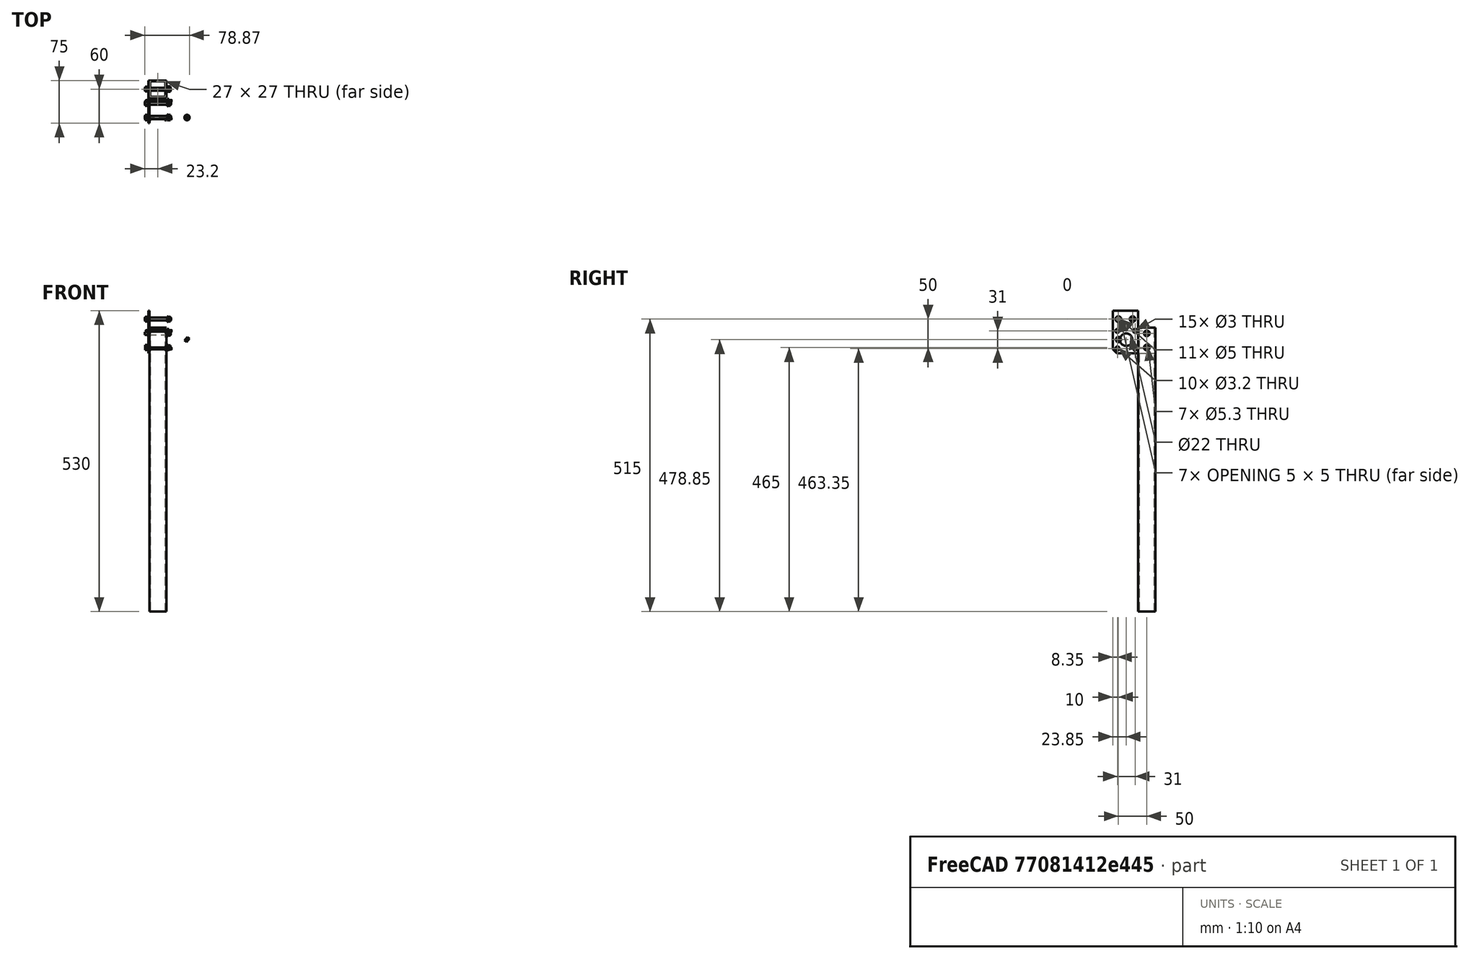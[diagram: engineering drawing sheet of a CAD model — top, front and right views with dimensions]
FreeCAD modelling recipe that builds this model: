
FCSTD DOCUMENT  (FreeCAD 0.21R33694 (Git))
Label: example
License: All rights reserved
LicenseURL: http://en.wikipedia.org/wiki/All_rights_reserved
objects: Part::FeaturePython×49, Part::Feature×18, App::DocumentObjectGroupPython×16, Part::Cylinder×1, PartDesign::Pocket×1, Part::Thickness×1
note: 71 computed .brp shape members not serialized (recipe doc carries the construction recipe); baked Part::Feature solids carry a one-line shape summary decoded from their .brp

FEATURE [Part::FeaturePython] Clone053  label="Clone of Hexagon nut ISO4032 - M010"  # WARN: FeaturePython — macro-defined, semantics opaque (R4)
  Placement = pos=(53.1534,405,-17.3076) rot=(0,-1,0;0.890118rad)
  Scale = (1,1,1)
FEATURE [Part::FeaturePython] Clone062  label="Clone of Clone of Clone of Clone of Clone of Plain washer ISO7089 - M010"  # WARN: FeaturePython — macro-defined, semantics opaque (R4)
  Placement = pos=(17.5,405,20) rot=(0.57735,0.57735,-0.57735;4.18879rad)
  Scale = (1,1,1)
FEATURE [Part::Cylinder] Cylinder001  label="Cilindro001"
  Angle = 360
  AttacherType = Attacher::AttachEngine3D
  FirstAngle = 0
  Height = 45
  Placement = pos=(-21,403.35,-0.65) rot=(0.57735,-0.57735,0.57735;4.18879rad)
  Radius = 1.5
  SecondAngle = 0
FEATURE [Part::FeaturePython] Clone029  label="Clone of Cilindro005"  # Draft clone (typed FeaturePython)
  Objects = -> [Cylinder001]
  Placement = pos=(-21,403.35,-31.65) rot=(0.57735,-0.57735,0.57735;4.18879rad)
  Scale = (1,1,1)
FEATURE [Part::Feature] BOLTS_part002  label="Hexagon nut ISO4032 - M3"
  Placement = pos=(17,434.35,-31.65) rot=(-0.383062,-0.840552,-0.383062;4.53956rad)
  shape: bbox 2.4 x 6.234 x 6.005 mm, 9 faces (baked)
FEATURE [Part::FeaturePython] Clone068  label="Clone of Hexagon nut ISO4032 - M014"  # Draft clone (typed FeaturePython)
  Objects = -> [BOLTS_part002]
  Placement = pos=(19.4,403.35,-0.65) rot=(-0.383062,0.840552,0.383062;4.53956rad)
  Scale = (1,1,1)
FEATURE [Part::FeaturePython] Clone081  label="Clone of Hexagon nut ISO4032 - M020"  # Draft clone (typed FeaturePython)
  Objects = -> [BOLTS_part002]
  Placement = pos=(19.4,403.35,-31.65) rot=(-0.383062,0.840552,0.383062;4.53956rad)
  Scale = (1,1,1)
FEATURE [Part::Feature] BOLTS_part004  label="Plain washer ISO7089 - M3"
  Placement = pos=(17,434.35,-31.65) rot=(0,-1,0;1.5708rad)
  shape: bbox 0.5 x 7 x 7 mm, 4 faces (baked)
FEATURE [Part::FeaturePython] Clone074  label="Clone of Plain washer ISO7089 - M3"  # Draft clone (typed FeaturePython)
  Objects = -> [BOLTS_part004]
  Placement = pos=(17,403.35,-0.65) rot=(0,-1,0;1.5708rad)
  Scale = (1,1,1)
FEATURE [Part::FeaturePython] Clone080  label="Clone of Plain washer ISO7089 - M012"  # Draft clone (typed FeaturePython)
  Objects = -> [BOLTS_part004]
  Placement = pos=(17,403.35,-31.65) rot=(0,-1,0;1.5708rad)
  Scale = (1,1,1)
FEATURE [Part::FeaturePython] Clone031  label="Clone of Cilindro007"  # Draft clone (typed FeaturePython)
  Objects = -> [Cylinder001]
  Placement = pos=(-21,434.35,-31.65) rot=(0.57735,-0.57735,0.57735;4.18879rad)
  Scale = (1,1,1)
FEATURE [Part::FeaturePython] Clone030  label="Clone of Cilindro006"  # Draft clone (typed FeaturePython)
  Objects = -> [Cylinder001]
  Placement = pos=(-21,434.35,-0.65) rot=(0.57735,-0.57735,0.57735;4.18879rad)
  Scale = (1,1,1)
FEATURE [Part::FeaturePython] Clone067  label="Clone of Hexagon nut ISO4032 - M3"  # Draft clone (typed FeaturePython)
  Objects = -> [BOLTS_part002]
  Placement = pos=(19.4,434.35,-0.65) rot=(-0.383062,0.840552,0.383062;4.53956rad)
  Scale = (1,1,1)
FEATURE [Part::FeaturePython] Clone075  label="Clone of Plain washer ISO7089 - M007"  # Draft clone (typed FeaturePython)
  Objects = -> [BOLTS_part004]
  Placement = pos=(17,434.35,-0.65) rot=(0,-1,0;1.5708rad)
  Scale = (1,1,1)
FEATURE [Part::FeaturePython] Clone090  # WARN: FeaturePython — macro-defined, semantics opaque (R4)
FEATURE [Part::FeaturePython] Clone050  label="Clone of Hexagon nut ISO4032 - M007"  # WARN: FeaturePython — macro-defined, semantics opaque (R4)
  Placement = pos=(22.2,430,20) rot=(0,1,0;4.71239rad)
  Scale = (1,1,1)
FEATURE [Part::FeaturePython] Clone061  label="Clone of Clone of Clone of Clone of Clone of Plain washer ISO7089 - M009"  # WARN: FeaturePython — macro-defined, semantics opaque (R4)
  Placement = pos=(17.5,430,20) rot=(0,-1,0;1.5708rad)
  Scale = (1,1,1)
FEATURE [Part::FeaturePython] Clone052  label="Clone of Hexagon nut ISO4032 - M009"  # WARN: FeaturePython — macro-defined, semantics opaque (R4)
  Placement = pos=(22.2,455,-5) rot=(0,1,0;4.71239rad)
  Scale = (1,1,1)
FEATURE [Part::FeaturePython] Clone060  label="Clone of Clone of Clone of Clone of Clone of Plain washer ISO7089 - M008"  # WARN: FeaturePython — macro-defined, semantics opaque (R4)
  Placement = pos=(17.5,455,-5) rot=(0,-1,0;1.5708rad)
  Scale = (1,1,1)
FEATURE [Part::FeaturePython] Clone051  label="Clone of Hexagon nut ISO4032 - M008"  # WARN: FeaturePython — macro-defined, semantics opaque (R4)
  Placement = pos=(22.2,455,-30) rot=(0,1,0;4.71239rad)
  Scale = (1,1,1)
FEATURE [Part::FeaturePython] Clone059  label="Clone of Clone of Clone of Clone of Clone of Plain washer ISO7089 - M007"  # WARN: FeaturePython — macro-defined, semantics opaque (R4)
  Placement = pos=(17.5,455,-30) rot=(0,-1,0;1.5708rad)
  Scale = (1,1,1)
FEATURE [Part::FeaturePython] Clone089  label="Clone of Clone of Cilindro003"  # WARN: FeaturePython — macro-defined, semantics opaque (R4)
  Placement = pos=(-22.8,455,-30) rot=(0,1,0;1.5708rad)
  Scale = (1,1,1)
FEATURE [Part::FeaturePython] Clone091  label="Clone of Clone of Clone of Cilindro004"  # Draft clone (typed FeaturePython)
  Objects = -> [Clone089]
  Placement = pos=(-22.8,405,20) rot=(0,1,0;1.5708rad)
  Scale = (1,1,1)
FEATURE [Part::FeaturePython] Clone092  label="Clone of Clone of Clone of Cilindro005"  # Draft clone (typed FeaturePython)
  Objects = -> [Clone089]
  Placement = pos=(-23.2,455,-5) rot=(0,1,0;1.5708rad)
  Scale = (1,1,1)
FEATURE [PartDesign::Pocket] Pocket005
  AllowMultiFace = false
  Direction = (1,1,1)
  Length = 5
  Length2 = 5
  Placement = pos=(16.1113,-0.661292,-3.33e-14) rot=(-0.57735,0.57735,0.57735;4.18879rad)
  Type = 0
FEATURE [Part::FeaturePython] Clone028  label="Clone of Pocket005"  # Draft clone (typed FeaturePython)
  Objects = -> [Pocket005]
  Placement = pos=(-15,0,0) rot=(0.57735,-0.57735,-0.57735;2.0944rad)
  Scale = (1,1,1)
FEATURE [Part::FeaturePython] Clone076  label="Clone of Plain washer ISO7089 - M008"  # Draft clone (typed FeaturePython)
  Objects = -> [BOLTS_part004]
  Placement = pos=(15,403.35,-31.65) rot=(0,-1,0;1.5708rad)
  Scale = (1,1,1)
FEATURE [Part::FeaturePython] Clone070  label="Clone of Hexagon nut ISO4032 - M016"  # Draft clone (typed FeaturePython)
  Objects = -> [BOLTS_part002]
  Placement = pos=(14.5,403.35,-31.65) rot=(0,-1,0;1.5708rad)
  Scale = (1,1,1)
FEATURE [Part::FeaturePython] Clone078  label="Clone of Plain washer ISO7089 - M010"  # Draft clone (typed FeaturePython)
  Objects = -> [BOLTS_part004]
  Placement = pos=(15,434.35,-31.65) rot=(0,-1,0;1.5708rad)
  Scale = (1,1,1)
FEATURE [Part::FeaturePython] Clone069  label="Clone of Hexagon nut ISO4032 - M015"  # Draft clone (typed FeaturePython)
  Objects = -> [BOLTS_part002]
  Placement = pos=(14.5,434.35,-31.65) rot=(0,-1,0;1.5708rad)
  Scale = (1,1,1)
FEATURE [Part::FeaturePython] Clone079  label="Clone of Plain washer ISO7089 - M011"  # Draft clone (typed FeaturePython)
  Objects = -> [BOLTS_part004]
  Placement = pos=(15,434.35,-0.65) rot=(0,-1,0;1.5708rad)
  Scale = (1,1,1)
FEATURE [Part::FeaturePython] Clone072  label="Clone of Hexagon nut ISO4032 - M018"  # Draft clone (typed FeaturePython)
  Objects = -> [BOLTS_part002]
  Placement = pos=(14.5,434.35,-0.65) rot=(0,-1,0;1.5708rad)
  Scale = (1,1,1)
FEATURE [Part::FeaturePython] Clone077  label="Clone of Plain washer ISO7089 - M009"  # Draft clone (typed FeaturePython)
  Objects = -> [BOLTS_part004]
  Placement = pos=(15,403.35,-0.65) rot=(0,-1,0;1.5708rad)
  Scale = (1,1,1)
FEATURE [Part::FeaturePython] Clone071  label="Clone of Hexagon nut ISO4032 - M017"  # Draft clone (typed FeaturePython)
  Objects = -> [BOLTS_part002]
  Placement = pos=(14.5,403.35,-0.65) rot=(0,-1,0;1.5708rad)
  Scale = (1,1,1)
FEATURE [Part::FeaturePython] Clone087  label="Clone of Clone of Hexagon nut ISO4032 - M020"  # WARN: FeaturePython — macro-defined, semantics opaque (R4)
  Placement = pos=(-12.1,403.35,-31.65) rot=(0,1,0;4.71239rad)
  Scale = (1,1,1)
FEATURE [Part::FeaturePython] Clone088  label="Clone of Clone of Hexagon nut ISO4032 - M021"  # WARN: FeaturePython — macro-defined, semantics opaque (R4)
  Placement = pos=(-12.1,434.35,-31.65) rot=(0,1,0;4.71239rad)
  Scale = (1,1,1)
FEATURE [Part::FeaturePython] Clone082  label="Clone of Clone of Plain washer ISO7089 - M012"  # Draft clone (typed FeaturePython)
  Objects = -> [Clone080]
  Placement = pos=(-14.5,434.35,-31.65) rot=(0,-1,0;1.5708rad)
  Scale = (1,1,1)
FEATURE [Part::FeaturePython] Clone085  label="Clone of Clone of Plain washer ISO7089 - M015"  # Draft clone (typed FeaturePython)
  Objects = -> [Clone080]
  Placement = pos=(-14.5,403.35,-0.65) rot=(0,-1,0;1.5708rad)
  Scale = (1,1,1)
FEATURE [Part::Feature] Fusion002  label="Nema17+Pulley002"
  Placement = pos=(-63.5,418.85,-16.15) rot=(1,0,0;3.14159rad)
  shape: bbox 71 x 42.3 x 42.3 mm, 115 faces (baked)
FEATURE [Part::FeaturePython] Clone056  label="Clone of Hexagon nut ISO4032 - M013"  # WARN: FeaturePython — macro-defined, semantics opaque (R4)
  Placement = pos=(-22.2,455,-30) rot=(0.185846,-0.964843,0.185846;4.67661rad)
  Scale = (1,1,1)
FEATURE [Part::FeaturePython] Clone054  label="Clone of Hexagon nut ISO4032 - M011"  # WARN: FeaturePython — macro-defined, semantics opaque (R4)
  Placement = pos=(-17.5,455,-5) rot=(0,1,0;4.71239rad)
  Scale = (1,1,1)
FEATURE [Part::FeaturePython] Clone057  label="Clone of Clone of Hexagon nut ISO4032 - M011"  # Draft clone (typed FeaturePython)
  Objects = -> [Clone054]
  Placement = pos=(-17.5,405,20) rot=(0,1,0;4.71239rad)
  Scale = (1,1,1)
FEATURE [Part::FeaturePython] Clone063  label="Clone of Clone of Clone of Clone of Clone of Plain washer ISO7089 - M011"  # WARN: FeaturePython — macro-defined, semantics opaque (R4)
  Placement = pos=(-16.5,405,20) rot=(0,-1,0;1.5708rad)
  Scale = (1,1,1)
FEATURE [Part::FeaturePython] Clone093  label="Clone of Clone of Clone of Cilindro003"  # Draft clone (typed FeaturePython)
  Objects = -> [Clone089]
  Placement = pos=(-22.8,430,20) rot=(0,1,0;1.5708rad)
  Scale = (1,1,1)
FEATURE [Part::FeaturePython] Clone055  label="Clone of Hexagon nut ISO4032 - M012"  # WARN: FeaturePython — macro-defined, semantics opaque (R4)
  Placement = pos=(-17.5,430,20) rot=(0,1,0;4.71239rad)
  Scale = (1,1,1)
FEATURE [Part::FeaturePython] Clone064  label="Clone of Clone of Clone of Clone of Clone of Plain washer ISO7089 - M012"  # WARN: FeaturePython — macro-defined, semantics opaque (R4)
  Placement = pos=(-16.5,430,20) rot=(0,-1,0;1.5708rad)
  Scale = (1,1,1)
FEATURE [Part::FeaturePython] Clone065  label="Clone of Clone of Clone of Clone of Clone of Clone of Plain washer ISO7089 - M012"  # Draft clone (typed FeaturePython)
  Objects = -> [Clone064]
  Placement = pos=(-16.5,455,-30) rot=(0,-1,0;1.5708rad)
  Scale = (1,1,1)
FEATURE [Part::FeaturePython] Clone066  label="Clone of Clone of Clone of Clone of Clone of Clone of Plain washer ISO7089 - M013"  # Draft clone (typed FeaturePython)
  Objects = -> [Clone064]
  Placement = pos=(-16.5,455,-5) rot=(0,-1,0;1.5708rad)
  Scale = (1,1,1)
FEATURE [Part::Thickness] Thickness
  Intersection = false
  Join = 0
  Mode = 0
  SelfIntersection = false
  Value = -1.5
FEATURE [Part::FeaturePython] Clone023  label="Clone of Thickness001"  # Draft clone (typed FeaturePython)
  Objects = -> [Thickness]
  Placement = pos=(0,475,-465) rot=(1,0,0;1.5708rad)
  Scale = (1,1,1)
FEATURE [Part::FeaturePython] Clone094  label="Clone of Hexagon nut ISO4032 - M021"  # WARN: FeaturePython — macro-defined, semantics opaque (R4)
  Placement = pos=(22.2,405,20) rot=(0,1,0;4.71239rad)
  Scale = (1,1,1)
FEATURE [Part::FeaturePython] Clone095  label="Clone of Clone of Plain washer ISO7089 - M016"  # Draft clone (typed FeaturePython)
  Objects = -> [Clone080]
  Placement = pos=(-14.5,434.35,-0.65) rot=(0,-1,0;1.5708rad)
  Scale = (1,1,1)
FEATURE [Part::FeaturePython] Clone096  label="Clone of Clone of Plain washer ISO7089 - M017"  # Draft clone (typed FeaturePython)
  Objects = -> [Clone080]
  Placement = pos=(-14.5,403.35,-31.65) rot=(0,-1,0;1.5708rad)
  Scale = (1,1,1)
FEATURE [Part::FeaturePython] Clone097  label="Clone of Hexagon nut ISO4032 - M022"  # Draft clone (typed FeaturePython)
  Objects = -> [BOLTS_part002]
  Placement = pos=(-12.1,434.35,-0.65) rot=(0,1,0;4.71239rad)
  Scale = (1,1,1)
FEATURE [Part::FeaturePython] Clone098  label="Clone of Hexagon nut ISO4032 - M023"  # Draft clone (typed FeaturePython)
  Objects = -> [BOLTS_part002]
  Placement = pos=(-12.1,403.35,-0.65) rot=(0,1,0;4.71239rad)
  Scale = (1,1,1)
FEATURE [Part::Feature] trajectory_line
  shape: bbox 10 x 31 x 31 mm, 0 faces, 0 solids (baked)
FEATURE [App::DocumentObjectGroupPython] BoltGroup  # scripted group (container) (typed FeaturePython)
  AnimationStepTime = 0
  AnimationSteps = 60
  Distance = 10
  Group = -> [trajectory_line]
  Revolutions = 1
  dir_vectors = (4) [(1,-3.69779e-32,-3.33067e-16),(1,-3.69779e-32,-3.33067e-16),(1,-3.69779e-32,-3.33067e-16),(1,-3.69779e-32,-3.33067e-16)]
  rot_centers = (4) [(19.4,434.35,-0.65),(19.4,434.35,-31.65),(19.4,403.35,-31.65),(19.4,403.35,-0.65)]
  rot_vectors = (4) [(1,-3.69779e-32,-3.33067e-16),(1,-3.69779e-32,-3.33067e-16),(1,-3.69779e-32,-3.33067e-16),(1,-3.69779e-32,-3.33067e-16)]
FEATURE [Part::Feature] trajectory_line001
  shape: bbox 50 x 2e-07 x 2e-07 mm, 0 faces, 0 solids (baked)
FEATURE [App::DocumentObjectGroupPython] SimpleGroup  # scripted group (container) (typed FeaturePython)
  AnimationStepTime = 0
  AnimationSteps = 20
  Distance = 50
  Group = -> [trajectory_line001]
  Revolutions = 0
  dir_vectors = (4) [(1,-3.69779e-32,-3.33067e-16),(1,-3.69779e-32,-3.33067e-16),(1,-3.69779e-32,-3.33067e-16),(1,-3.69779e-32,-3.33067e-16)]
  rot_centers = (4) [(16.5,429.152,-5.84829),(16.5,429.152,-5.84829),(16.5,429.152,-5.84829),(16.5,429.152,-5.84829)]
  rot_vectors = (4) [(1,-3.69779e-32,-3.33067e-16),(1,-3.69779e-32,-3.33067e-16),(1,-3.69779e-32,-3.33067e-16),(1,-3.69779e-32,-3.33067e-16)]
FEATURE [Part::Feature] trajectory_line002
  shape: bbox 50 x 2e-07 x 2e-07 mm, 0 faces, 0 solids (baked)
FEATURE [App::DocumentObjectGroupPython] SimpleGroup001  # scripted group (container) (typed FeaturePython)
  AnimationStepTime = 0
  AnimationSteps = 20
  Distance = 50
  Group = -> [trajectory_line002]
  Revolutions = 0
  dir_vectors = (4) [(1,-3.69779e-32,-3.33067e-16),(1,-3.69779e-32,-3.33067e-16),(1,-3.69779e-32,-3.33067e-16),(1,-3.69779e-32,-3.33067e-16)]
  rot_centers = (4) [(16.5,429.152,-5.84829),(16.5,429.152,-5.84829),(16.5,429.152,-5.84829),(16.5,429.152,-5.84829)]
  rot_vectors = (4) [(1,-3.69779e-32,-3.33067e-16),(1,-3.69779e-32,-3.33067e-16),(1,-3.69779e-32,-3.33067e-16),(1,-3.69779e-32,-3.33067e-16)]
FEATURE [Part::Feature] trajectory_line003
  shape: bbox 20 x 31 x 31 mm, 0 faces, 0 solids (baked)
FEATURE [App::DocumentObjectGroupPython] BoltGroup001  # scripted group (container) (typed FeaturePython)
  AnimationStepTime = 0
  AnimationSteps = 60
  Distance = 20
  Group = -> [trajectory_line003]
  Revolutions = 3
  dir_vectors = (4) [(1,-3.69779e-32,-3.33067e-16),(1,-3.69779e-32,-3.33067e-16),(1,-3.69779e-32,-3.33067e-16),(1,-3.69779e-32,-3.33067e-16)]
  rot_centers = (4) [(-12.1,434.35,-31.65),(-12.1,403.35,-31.65),(-12.1,434.35,-0.65),(-12.1,403.35,-0.65)]
  rot_vectors = (4) [(1,-3.69779e-32,-3.33067e-16),(1,-3.69779e-32,-3.33067e-16),(1,-3.69779e-32,-3.33067e-16),(1,-3.69779e-32,-3.33067e-16)]
FEATURE [Part::Feature] trajectory_line004
  shape: bbox 50 x 50 x 50 mm, 0 faces, 0 solids (baked)
FEATURE [App::DocumentObjectGroupPython] BoltGroup002  # scripted group (container) (typed FeaturePython)
  AnimationStepTime = 0
  AnimationSteps = 20
  Distance = 50
  Group = -> [trajectory_line004]
  Revolutions = 1
  dir_vectors = (4) [(1,-3.69779e-32,-3.33067e-16),(1,-3.69779e-32,-3.33067e-16),(1,-3.69779e-32,-3.33067e-16),(1,-3.69779e-32,-3.33067e-16)]
  rot_centers = (4) [(22.2,455,-30),(22.2,455,-5),(22.2,430,20),(22.2,405,20)]
  rot_vectors = (4) [(1,-3.69779e-32,-3.33067e-16),(1,-3.69779e-32,-3.33067e-16),(1,-3.69779e-32,-3.33067e-16),(1,-3.69779e-32,-3.33067e-16)]
FEATURE [Part::Feature] trajectory_line005
  shape: bbox 40 x 2e-07 x 2e-07 mm, 0 faces, 0 solids (baked)
FEATURE [App::DocumentObjectGroupPython] SimpleGroup002  # scripted group (container) (typed FeaturePython)
  AnimationStepTime = 0
  AnimationSteps = 20
  Distance = 40
  Group = -> [trajectory_line005]
  Revolutions = 0
  dir_vectors = (4) [(1,-3.69779e-32,-3.33067e-16),(1,-3.69779e-32,-3.33067e-16),(1,-3.69779e-32,-3.33067e-16),(1,-3.69779e-32,-3.33067e-16)]
  rot_centers = (4) [(16.5,429.152,-5.84829),(16.5,429.152,-5.84829),(16.5,429.152,-5.84829),(16.5,429.152,-5.84829)]
  rot_vectors = (4) [(1,-3.69779e-32,-3.33067e-16),(1,-3.69779e-32,-3.33067e-16),(1,-3.69779e-32,-3.33067e-16),(1,-3.69779e-32,-3.33067e-16)]
FEATURE [Part::Feature] trajectory_line006
  shape: bbox 60 x 2e-07 x 2e-07 mm, 0 faces, 0 solids (baked)
FEATURE [App::DocumentObjectGroupPython] SimpleGroup003  # scripted group (container) (typed FeaturePython)
  AnimationStepTime = 0
  AnimationSteps = 20
  Distance = 60
  Group = -> [trajectory_line006]
  Revolutions = 0
  dir_vectors = (1) [(-1,-8.65956e-17,-2.22045e-16)]
  rot_centers = (1) [(1.1,418.85,-16.15)]
  rot_vectors = (1) [(-1,-8.65956e-17,-2.22045e-16)]
FEATURE [Part::Feature] trajectory_line007
  shape: bbox 20 x 2e-07 x 2e-07 mm, 0 faces, 0 solids (baked)
FEATURE [App::DocumentObjectGroupPython] SimpleGroup004  # scripted group (container) (typed FeaturePython)
  AnimationStepTime = 0
  AnimationSteps = 20
  Distance = 20
  Group = -> [trajectory_line007]
  Revolutions = 0
  dir_vectors = (1) [(1,-3.69779e-32,-3.33067e-16)]
  rot_centers = (1) [(16.5,429.152,-5.84829)]
  rot_vectors = (1) [(1,-3.69779e-32,-3.33067e-16)]
FEATURE [Part::Feature] trajectory_line008
  shape: bbox 2e-07 x 80 x 2e-07 mm, 0 faces, 0 solids (baked)
FEATURE [App::DocumentObjectGroupPython] SimpleGroup005  # scripted group (container) (typed FeaturePython)
  AnimationStepTime = 0
  AnimationSteps = 20
  Distance = 80
  Group = -> [trajectory_line008]
  Revolutions = 0
  dir_vectors = (1) [(-7.39557e-32,1,-3.33067e-16)]
  rot_centers = (1) [(35.75,470,-17.5)]
  rot_vectors = (1) [(-7.39557e-32,1,-3.33067e-16)]
FEATURE [Part::Feature] trajectory_line009
  shape: bbox 2e-07 x 1 x 2e-07 mm, 0 faces, 0 solids (baked)
FEATURE [App::DocumentObjectGroupPython] SimpleGroup006  # scripted group (container) (typed FeaturePython)
  AnimationStepTime = 0
  AnimationSteps = 20
  Distance = 1
  Group = -> [trajectory_line009]
  Revolutions = -0.25
  dir_vectors = (1) [(0,1,0)]
  rot_centers = (1) [(35.75,475,1)]
  rot_vectors = (1) [(0,0,1)]
FEATURE [Part::Feature] trajectory_line010
  shape: bbox 50 x 50 x 50 mm, 0 faces, 0 solids (baked)
FEATURE [App::DocumentObjectGroupPython] BoltGroup003  # scripted group (container) (typed FeaturePython)
  AnimationStepTime = 0
  AnimationSteps = 50
  Distance = 50
  Group = -> [trajectory_line010]
  Revolutions = 5
  dir_vectors = (4) [(-1,0,0),(-1,0,0),(-1,0,0),(-1,0,0)]
  rot_centers = (4) [(-22.2,455,-30),(-22.2,455,-5),(-22.2,430,20),(-22.2,405,20)]
  rot_vectors = (4) [(-1,0,0),(-1,0,0),(-1,0,0),(-1,0,0)]
FEATURE [Part::Feature] trajectory_line011
  shape: bbox 20 x 50 x 50 mm, 0 faces, 0 solids (baked)
FEATURE [App::DocumentObjectGroupPython] BoltGroup004  # scripted group (container) (typed FeaturePython)
  AnimationStepTime = 0
  AnimationSteps = 20
  Distance = 20
  Group = -> [trajectory_line011]
  Revolutions = 0
  dir_vectors = (4) [(-1,0,0),(-1,0,0),(-1,0,0),(-1,0,0)]
  rot_centers = (4) [(-17.5,455,-5),(-17.5,455,-30),(-17.5,430,20),(-17.5,405,20)]
  rot_vectors = (4) [(-1,0,0),(-1,0,0),(-1,0,0),(-1,0,0)]
FEATURE [Part::Feature] trajectory_line012
  shape: bbox 20 x 2e-07 x 2e-07 mm, 0 faces, 0 solids (baked)
FEATURE [App::DocumentObjectGroupPython] SimpleGroup007  # scripted group (container) (typed FeaturePython)
  AnimationStepTime = 0
  AnimationSteps = 20
  Distance = 20
  Group = -> [trajectory_line012]
  Revolutions = 0
  dir_vectors = (1) [(-1,0,0)]
  rot_centers = (1) [(-16.5,429.152,-5.84829)]
  rot_vectors = (1) [(-1,0,0)]
FEATURE [Part::Feature] trajectory_line013
  shape: bbox 2e-07 x 100 x 2e-07 mm, 0 faces, 0 solids (baked)
FEATURE [App::DocumentObjectGroupPython] SimpleGroup008  # scripted group (container) (typed FeaturePython)
  AnimationStepTime = 0
  AnimationSteps = 20
  Distance = 100
  Group = -> [trajectory_line013]
  Revolutions = 0
  dir_vectors = (1) [(0,-1,1.1e-16)]
  rot_centers = (1) [(-35.75,395,1)]
  rot_vectors = (1) [(0,-1,1.1e-16)]
FEATURE [Part::Feature] trajectory_line014
  shape: bbox 20 x 2e-07 x 2e-07 mm, 0 faces, 0 solids (baked)
FEATURE [App::DocumentObjectGroupPython] SimpleGroup009  # scripted group (container) (typed FeaturePython)
  AnimationStepTime = 0
  AnimationSteps = 20
  Distance = 50
  Group = -> [trajectory_line014]
  Revolutions = 0
  dir_vectors = (1) [(-1,0,0)]
  rot_centers = (1) [(-36.5,329.152,-5.84829)]
  rot_vectors = (1) [(-1,0,0)]
FEATURE [App::DocumentObjectGroupPython] ExplodedAssembly  # scripted group (container) (typed FeaturePython)
  AnimationStep = 0
  CurrentTrajectory = 0
  Group = -> [BoltGroup,SimpleGroup,SimpleGroup001,BoltGroup001,BoltGroup002,SimpleGroup002,SimpleGroup003,SimpleGroup004,SimpleGroup005,SimpleGroup006,BoltGroup003,BoltGroup004,SimpleGroup007,SimpleGroup008,SimpleGroup009]
  InAnimation = false
  RemoveAllTrajectories = false
  ResetAnimation = false
